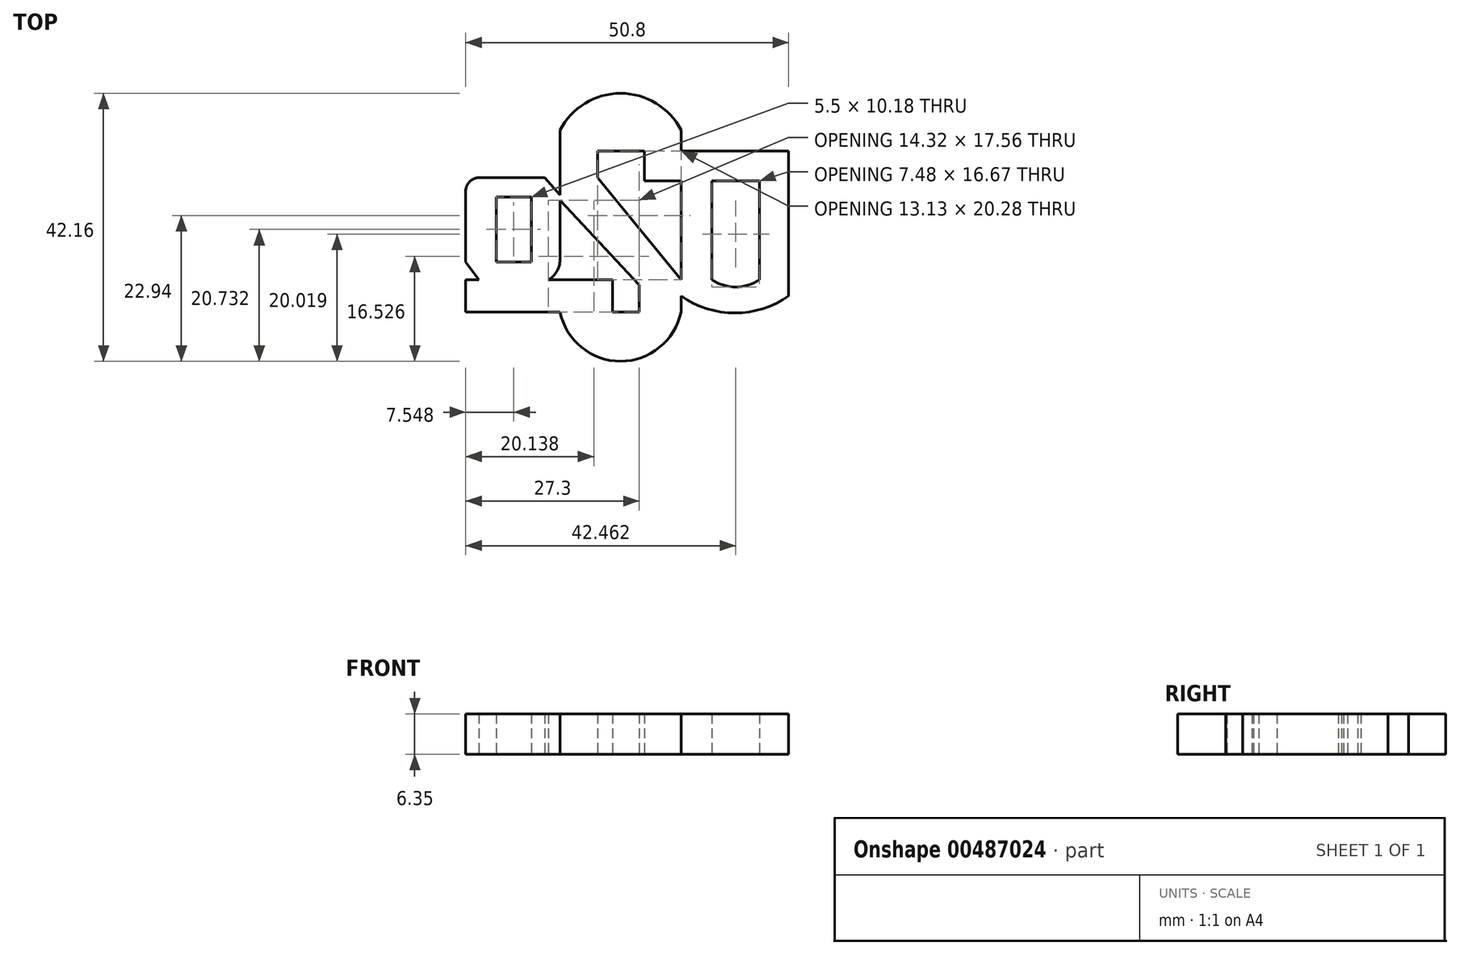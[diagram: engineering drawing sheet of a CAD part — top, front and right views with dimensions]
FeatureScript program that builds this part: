
annotation { "Feature Type Name" : "Feature", "Feature Type Description" : "" }
export const myFeature = defineFeature(function(context is Context, id is Id, definition is map)
    precondition{}
    {
        {
            var Q0;
            Q0=qCreatedBy(makeId("Top.planeOp"),FACE);
            var sketch = newSketch(context, id + "F0", { "sketchPlane" : qUnion([Q0])});
            skLineSegment(sketch, "E0", {"start": v(-23.1, 0) * mm, "end": v(-21.02, 0) * mm});
            skPoint(sketch, "E1.startSnap0", {"position": v(-15.69, 16.08) * mm});
            skLineSegment(sketch, "E2", {"start": v(10.76, 23.56) * mm, "end": v(10.76, 20.28) * mm});
            skLineSegment(sketch, "E3", {"start": v(10.76, 20.28) * mm, "end": v(27.7, 20.28) * mm});
            skLineSegment(sketch, "E4", {"start": v(27.7, 20.28) * mm, "end": v(27.7, 15.56) * mm});
            skLineSegment(sketch, "E5", {"start": v(23.1, 15.56) * mm, "end": v(15.62, 15.56) * mm});
            skLineSegment(sketch, "E6", {"start": v(10.76, 15.56) * mm, "end": v(4.99, 15.56) * mm});
            skLineSegment(sketch, "E7", {"start": v(4.99, 15.56) * mm, "end": v(4.99, 20.28) * mm});
            skLineSegment(sketch, "E8", {"start": v(4.99, 20.28) * mm, "end": v(-2.36, 20.28) * mm});
            skLineSegment(sketch, "E9", {"start": v(-2.36, 20.28) * mm, "end": v(-2.36, 16.08) * mm});
            skLineSegment(sketch, "E10", {"start": v(-2.36, 16.08) * mm, "end": v(10.76, 0) * mm});
            skLineSegment(sketch, "E11", {"start": v(10.76, 0) * mm, "end": v(10.76, -5.05) * mm});
            skArc(sketch, "E12", {"start": v(-8.27, -5.05) * mm, "mid": v(1.25, -12.8) * mm, "end": v(10.76, -5.05) * mm});
            skLineSegment(sketch, "E13", {"start": v(-8.27, -5.05) * mm, "end": v(-23.1, -5.05) * mm});
            skPoint(sketch, "E13.endSnap0", {"position": v(-23.1, 8.04) * mm});
            skLineSegment(sketch, "E14", {"start": v(-23.1, -5.05) * mm, "end": v(-23.1, 0) * mm});
            skLineSegment(sketch, "E15", {"start": v(0, 0) * mm, "end": v(-10.12, 0) * mm});
            skLineSegment(sketch, "E16", {"start": v(0, 0) * mm, "end": v(0, -5.05) * mm});
            skLineSegment(sketch, "E17", {"start": v(0, -5.05) * mm, "end": v(4.2, -5.05) * mm});
            skLineSegment(sketch, "E18", {"start": v(4.2, -5.05) * mm, "end": v(4.2, -0.82) * mm});
            skArc(sketch, "E19", {"start": v(10.76, 23.56) * mm, "mid": v(1.25, 29.36) * mm, "end": v(-8.27, 23.56) * mm});
            skLineSegment(sketch, "E20", {"start": v(10.76, 15.56) * mm, "end": v(10.76, -2.53) * mm});
            skLineSegment(sketch, "E21", {"start": v(27.7, 15.56) * mm, "end": v(27.7, -2.53) * mm});
            skArc(sketch, "E22", {"start": v(10.76, -2.53) * mm, "mid": v(19.23, -5.2) * mm, "end": v(27.7, -2.53) * mm});
            skLineSegment(sketch, "E23", {"start": v(15.62, 15.56) * mm, "end": v(15.62, 0) * mm});
            skLineSegment(sketch, "E24", {"start": v(23.1, 15.56) * mm, "end": v(23.1, 0) * mm});
            skArc(sketch, "E25", {"start": v(15.62, 0) * mm, "mid": v(19.36, -1.12) * mm, "end": v(23.1, 0) * mm});
            skLineSegment(sketch, "E26", {"start": v(-23.1, 8.04) * mm, "end": v(-23.1, 12.14) * mm});
            skLineSegment(sketch, "E27", {"start": v(-20.04, 16.08) * mm, "end": v(-15.69, 16.08) * mm});
            skLineSegment(sketch, "E28", {"start": v(-23.1, 12.14) * mm, "end": v(-23.1, 13.96) * mm});
            skLineSegment(sketch, "E29", {"start": v(-20.04, 16.08) * mm, "end": v(-21.02, 16.08) * mm});
            skLineSegment(sketch, "E30", {"start": v(-15.69, 16.08) * mm, "end": v(-10.67, 16.08) * mm});
            skArc(sketch, "E31", {"start": v(-21.02, 16.08) * mm, "mid": v(-22.5, 15.46) * mm, "end": v(-23.1, 13.96) * mm});
            skLineSegment(sketch, "E32", {"start": v(-23.1, 8.04) * mm, "end": v(-23.1, 2.84) * mm});
            skPoint(sketch, "E32.endSnap0", {"position": v(-23.1, -2.53) * mm});
            skLineSegment(sketch, "E33", {"start": v(-23.1, 2.84) * mm, "end": v(-21.02, 0) * mm});
            skArc(sketch, "E34", {"start": v(-10.12, 0) * mm, "mid": v(-8.77, 1.34) * mm, "end": v(-8.27, 3.17) * mm});
            skLineSegment(sketch, "E35", {"start": v(-18.3, 2.84) * mm, "end": v(-12.8, 2.84) * mm});
            skLineSegment(sketch, "E36", {"start": v(-18.3, 13.02) * mm, "end": v(-12.8, 13.02) * mm});
            skLineSegment(sketch, "E37", {"start": v(-12.8, 13.02) * mm, "end": v(-12.8, 2.84) * mm});
            skLineSegment(sketch, "E38", {"start": v(-18.3, 2.84) * mm, "end": v(-18.3, 13.02) * mm});
            skArc(sketch, "E39", {"start": v(2.29, 29.31) * mm, "mid": v(1.12, 32.05) * mm, "end": v(0, 29.29) * mm});
            skCircle(sketch, "E40", {"center": v(1.13, 30.44) * mm, "radius": 0.81 * mm});
            skLineSegment(sketch, "E41", {"start": v(-10.67, 16.08) * mm, "end": v(-8.27, 13.32) * mm});
            skLineSegment(sketch, "E42", {"start": v(-8.27, 23.56) * mm, "end": v(-8.27, 13.32) * mm});
            skLineSegment(sketch, "E43", {"start": v(-8.27, 3.17) * mm, "end": v(-8.27, 12.5) * mm});
            skLineSegment(sketch, "E44.trimOffspring", {"start": v(-10.12, 0) * mm, "end": v(-8.27, 0) * mm});
            skLineSegment(sketch, "E45.trimOffspring", {"start": v(-21.02, 0) * mm, "end": v(-23.1, 0) * mm});
            skLineSegment(sketch, "E46.0", {"start": v(-8.27, 12.5) * mm, "end": v(4.2, -0.82) * mm});
            skPoint(sketch, "E47.orphan", {"position": v(4.69, -1.34) * mm});
            skPoint(sketch, "E48.orphan", {"position": v(4.2, 0) * mm});
            skPoint(sketch, "E49.orphan", {"position": v(-8.68, 12.94) * mm});
            skSolve(sketch);
        }
        {
            var Q0;
            Q0=makeQuery(id+"F0.imprint","IMPRINT",FACE,{"disambiguationData":[TD([[makeQuery(id+"F0.imprint","IMPRINT",EDGE,{"derivedFrom":sQuery(id+"F0.wireOp",EDGE,"E26")}),-1.0]])]});
            var Q1;
            {var subQ12=sQuery(id+"F0.wireOp",EDGE,"E2");Q1=makeQuery(id+"F0.imprint","IMPRINT",FACE,{"disambiguationData":[TD([[makeQuery(id+"F0.imprint","IMPRINT",EDGE,{"derivedFrom":subQ12}),-1.0]])]});}
            var Q2;
            {var subQ5=sQuery(id+"F0.wireOp",EDGE,"E21");Q2=makeQuery(id+"F0.imprint","IMPRINT",FACE,{"disambiguationData":[TD([[makeQuery(id+"F0.imprint","IMPRINT",EDGE,{"derivedFrom":subQ5}),-1.0]])]});}
            extrude(context, id + "F1", {"entities" : qUnion([Q0, Q1, Q2]), "depth" : 6.35 * mm});
        }
    });
